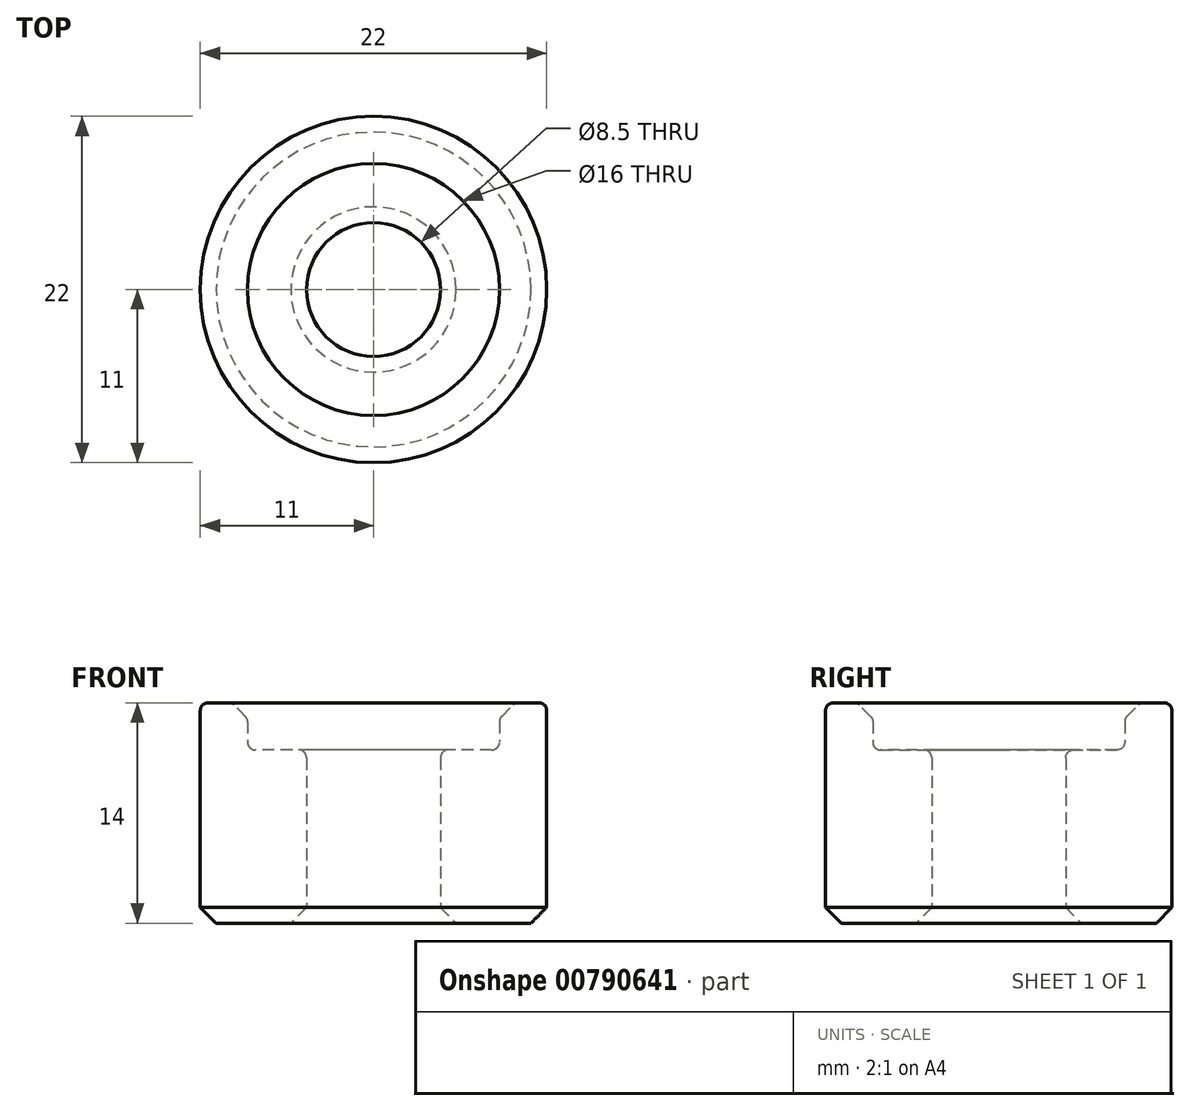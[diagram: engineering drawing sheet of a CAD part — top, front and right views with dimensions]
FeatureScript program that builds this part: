
annotation { "Feature Type Name" : "Feature", "Feature Type Description" : "" }
export const myFeature = defineFeature(function(context is Context, id is Id, definition is map)
    precondition{}
    {
        {
            var Q0;
            Q0=qCreatedBy(makeId("Top.planeOp"),FACE);
            var sketch = newSketch(context, id + "F0", { "sketchPlane" : qUnion([Q0])});
            skCircle(sketch, "E0", {"center": v(0, 0) * mm, "radius": 11 * mm});
            skCircle(sketch, "E1", {"center": v(0, 0) * mm, "radius": 8 * mm});
            skCircle(sketch, "E2", {"center": v(0, 0) * mm, "radius": 4.25 * mm});
            skSolve(sketch);
        }
        {
            var Q0;
            Q0 = qSketchRegion(id + "F0", true);
            var Q1;
            Q1=makeQuery(id+"F0.imprint","IMPRINT",FACE,{"disambiguationData":[TD([[makeQuery(id+"F0.imprint","IMPRINT",EDGE,{"derivedFrom":sQuery(id+"F0.wireOp",EDGE,"E1")}),1.0]])]});
            extrude(context, id + "F1", {"entities" : qUnion([Q0, Q1]), "depth" : 11 * mm, "offsetDistance" : 25 * mm});
        }
        {
            var Q0;
            Q0=makeQuery(id+"F0.imprint","IMPRINT",FACE,{"disambiguationData":[TD([[makeQuery(id+"F0.imprint","IMPRINT",EDGE,{"derivedFrom":sQuery(id+"F0.wireOp",EDGE,"E0")}),1.0]])]});
            extrude(context, id + "F2", {"entities" : qUnion([Q0]), "operationType" : NewBodyOperationType.ADD, "depth" : 14 * mm, "offsetDistance" : 25 * mm});
        }
        {
            var Q0;
            Q0=makeQuery(id+"F2.opExtrude","CAP_EDGE",EDGE,{"disambiguationData":[OSD([sQuery(id+"F0.wireOp",EDGE,"E1")])],"isStart":false});
            chamfer(context, id + "F3", {"entities" : qUnion([Q0]), "width" : 1 * mm, "tangentPropagation" : true});
        }
        {
            var Q0;
            {var subQ0=sQuery(id+"F0.wireOp",EDGE,"E1");Q0=makeQuery(id+"F3.opChamfer","BLEND_EDGE",EDGE,{"blendedFrom":[makeQuery(id+"F2.opExtrude","CAP_EDGE",EDGE,{"disambiguationData":[OSD([subQ0])],"isStart":false}),makeQuery(id+"F2.opExtrude","CAP_FACE",FACE,{"disambiguationData":[OSD([sQuery(id+"F0.wireOp",EDGE,"E0"),subQ0])],"isStart":false})],"blendedInto":[makeQuery(id+"F2.opExtrude","CAP_FACE",FACE,{"disambiguationData":[OSD([sQuery(id+"F0.wireOp",EDGE,"E0"),subQ0])],"isStart":false})]});}
            var Q1;
            {var subQ0=sQuery(id+"F0.wireOp",EDGE,"E1");Q1=makeQuery(id+"F3.opChamfer","BLEND_EDGE",EDGE,{"blendedFrom":[makeQuery(id+"F2.opExtrude","CAP_EDGE",EDGE,{"disambiguationData":[OSD([subQ0])],"isStart":false}),makeQuery(id+"F2.opExtrude","SWEPT_FACE",FACE,{"disambiguationData":[OSD([subQ0])]})],"blendedInto":[makeQuery(id+"F2.opExtrude","SWEPT_FACE",FACE,{"disambiguationData":[OSD([subQ0])]})]});}
            var Q2;
            Q2=makeQuery(id+"F2.opExtrude","CAP_EDGE",EDGE,{"disambiguationData":[OSD([sQuery(id+"F0.wireOp",EDGE,"E0")])],"isStart":false});
            var Q3;
            Q3=makeQuery(id+"F2.boolean.opBoolean","INTERSECT",EDGE,{"derivedFrom":[makeQuery(id+"F1.opExtrude","CAP_FACE",FACE,{"disambiguationData":[OSD([sQuery(id+"F0.wireOp",EDGE,"E0"),sQuery(id+"F0.wireOp",EDGE,"E2")])],"isStart":false}),makeQuery(id+"F2.opExtrude","SWEPT_FACE",FACE,{"disambiguationData":[OSD([sQuery(id+"F0.wireOp",EDGE,"E1")])]})]});
            var Q4;
            Q4=makeQuery(id+"F1.opExtrude","CAP_EDGE",EDGE,{"disambiguationData":[OSD([sQuery(id+"F0.wireOp",EDGE,"E2")])],"isStart":false});
            fillet(context, id + "F4", {"entities" : qUnion([Q0, Q1, Q2, Q3, Q4]), "radius" : .5 * mm, "tangentPropagation" : true, "allowEdgeOverflow" : false});
        }
        {
            var Q0;
            Q0=makeQuery(id+"F1.opExtrude","CAP_EDGE",EDGE,{"disambiguationData":[OSD([sQuery(id+"F0.wireOp",EDGE,"E0")])],"isStart":true});
            var Q1;
            Q1=makeQuery(id+"F1.opExtrude","CAP_EDGE",EDGE,{"disambiguationData":[OSD([sQuery(id+"F0.wireOp",EDGE,"E2")])],"isStart":true});
            chamfer(context, id + "F5", {"entities" : qUnion([Q0, Q1]), "width" : 1 * mm, "tangentPropagation" : true});
        }
    });
